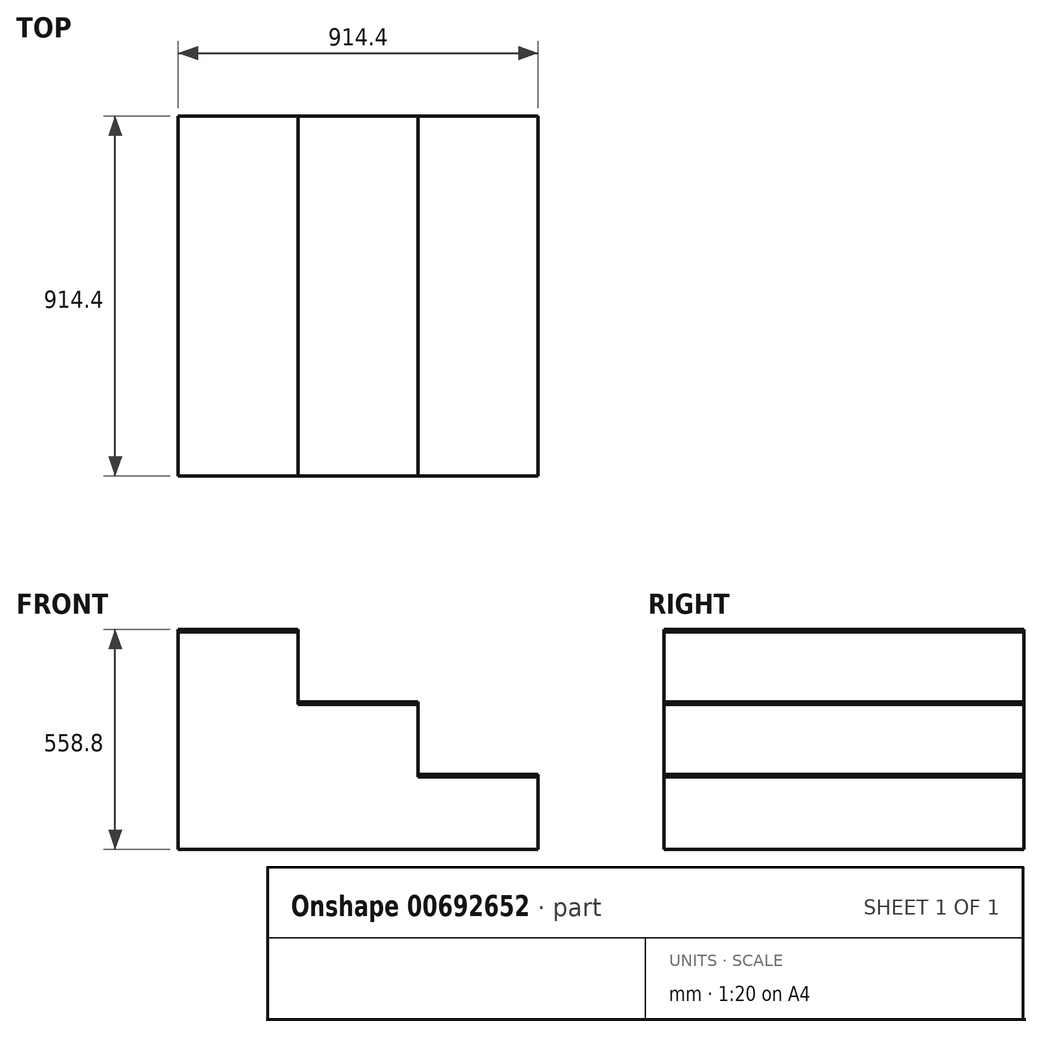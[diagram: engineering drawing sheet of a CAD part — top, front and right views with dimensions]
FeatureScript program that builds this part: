
annotation { "Feature Type Name" : "Feature", "Feature Type Description" : "" }
export const myFeature = defineFeature(function(context is Context, id is Id, definition is map)
    precondition{}
    {
        {
            var Q0;
            Q0=qCreatedBy(makeId("Top.planeOp"),FACE);
            var sketch = newSketch(context, id + "F0", { "sketchPlane" : qUnion([Q0])});
            skLineSegment(sketch, "E0.bottom", {"start": v(0, 0) * mm, "end": v(304.8, 0) * mm});
            skLineSegment(sketch, "E0.top", {"start": v(0, -914.4) * mm, "end": v(304.8, -914.4) * mm});
            skLineSegment(sketch, "E0.left", {"start": v(0, 0) * mm, "end": v(0, -914.4) * mm});
            skLineSegment(sketch, "E0.right", {"start": v(304.8, 0) * mm, "end": v(304.8, -914.4) * mm});
            skLineSegment(sketch, "E1.bottom", {"start": v(304.8, 0) * mm, "end": v(609.6, 0) * mm});
            skLineSegment(sketch, "E1.top", {"start": v(304.8, -914.4) * mm, "end": v(609.6, -914.4) * mm});
            skLineSegment(sketch, "E1.right", {"start": v(609.6, 0) * mm, "end": v(609.6, -914.4) * mm});
            skLineSegment(sketch, "E2.bottom", {"start": v(609.6, 0) * mm, "end": v(914.4, 0) * mm});
            skLineSegment(sketch, "E2.top", {"start": v(609.6, -914.4) * mm, "end": v(914.4, -914.4) * mm});
            skLineSegment(sketch, "E2.right", {"start": v(914.4, 0) * mm, "end": v(914.4, -914.4) * mm});
            skSolve(sketch);
        }
        {
            assignVariable(context, id + "F1", {"name" : "top_height", "anyValue" : 6.35 * mm});
        }
        {
            assignVariable(context, id + "F2", {"name" : "stair_height", "anyValue" : 190.5 * mm});
        }
        {
            var Q0;
            Q0=makeQuery(id+"F0.imprint","IMPRINT",FACE,{"disambiguationData":[TD([[makeQuery(id+"F0.imprint","IMPRINT",EDGE,{"derivedFrom":sQuery(id+"F0.wireOp",EDGE,"E0.bottom")}),-1.0]])]});
            extrude(context, id + "F3", {"entities" : qUnion([Q0]), "depth" : 3 * (getVariable(context, 'stair_height') - getVariable(context, 'top_height')), "offsetDistance" : 25.4 * mm});
        }
        {
            var Q0;
            Q0=makeQuery(id+"F0.imprint","IMPRINT",FACE,{"disambiguationData":[TD([[makeQuery(id+"F0.imprint","IMPRINT",EDGE,{"derivedFrom":sQuery(id+"F0.wireOp",EDGE,"E1.bottom")}),-1.0]])]});
            extrude(context, id + "F4", {"entities" : qUnion([Q0]), "operationType" : NewBodyOperationType.ADD, "depth" : 2 * (getVariable(context, 'stair_height') - getVariable(context, 'top_height')), "offsetDistance" : 25.4 * mm});
        }
        {
            var Q0;
            Q0=makeQuery(id+"F0.imprint","IMPRINT",FACE,{"disambiguationData":[TD([[makeQuery(id+"F0.imprint","IMPRINT",EDGE,{"derivedFrom":sQuery(id+"F0.wireOp",EDGE,"E2.bottom")}),-1.0]])]});
            extrude(context, id + "F5", {"entities" : qUnion([Q0]), "operationType" : NewBodyOperationType.ADD, "depth" : (getVariable(context, 'stair_height') - getVariable(context, 'top_height')), "offsetDistance" : 25.4 * mm});
        }
        {
            var Q0;
            Q0=makeQuery(id+"F3.opExtrude","CAP_FACE",FACE,{"disambiguationData":[OSD([sQuery(id+"F0.wireOp",EDGE,"E0.bottom"),sQuery(id+"F0.wireOp",EDGE,"E0.top"),sQuery(id+"F0.wireOp",EDGE,"E0.left"),sQuery(id+"F0.wireOp",EDGE,"E0.right")])],"isStart":false});
            var Q1;
            Q1=makeQuery(id+"F4.opExtrude","CAP_FACE",FACE,{"disambiguationData":[OSD([sQuery(id+"F0.wireOp",EDGE,"E1.bottom"),sQuery(id+"F0.wireOp",EDGE,"E1.top"),sQuery(id+"F0.wireOp",EDGE,"E0.right"),sQuery(id+"F0.wireOp",EDGE,"E1.right")])],"isStart":false});
            var Q2;
            Q2=makeQuery(id+"F5.opExtrude","CAP_FACE",FACE,{"disambiguationData":[OSD([sQuery(id+"F0.wireOp",EDGE,"E2.bottom"),sQuery(id+"F0.wireOp",EDGE,"E2.top"),sQuery(id+"F0.wireOp",EDGE,"E1.right"),sQuery(id+"F0.wireOp",EDGE,"E2.right")])],"isStart":false});
            extrude(context, id + "F6", {"entities" : qUnion([Q0, Q1, Q2]), "depth" : getVariable(context, 'top_height'), "offsetDistance" : 25.4 * mm});
        }
    });
